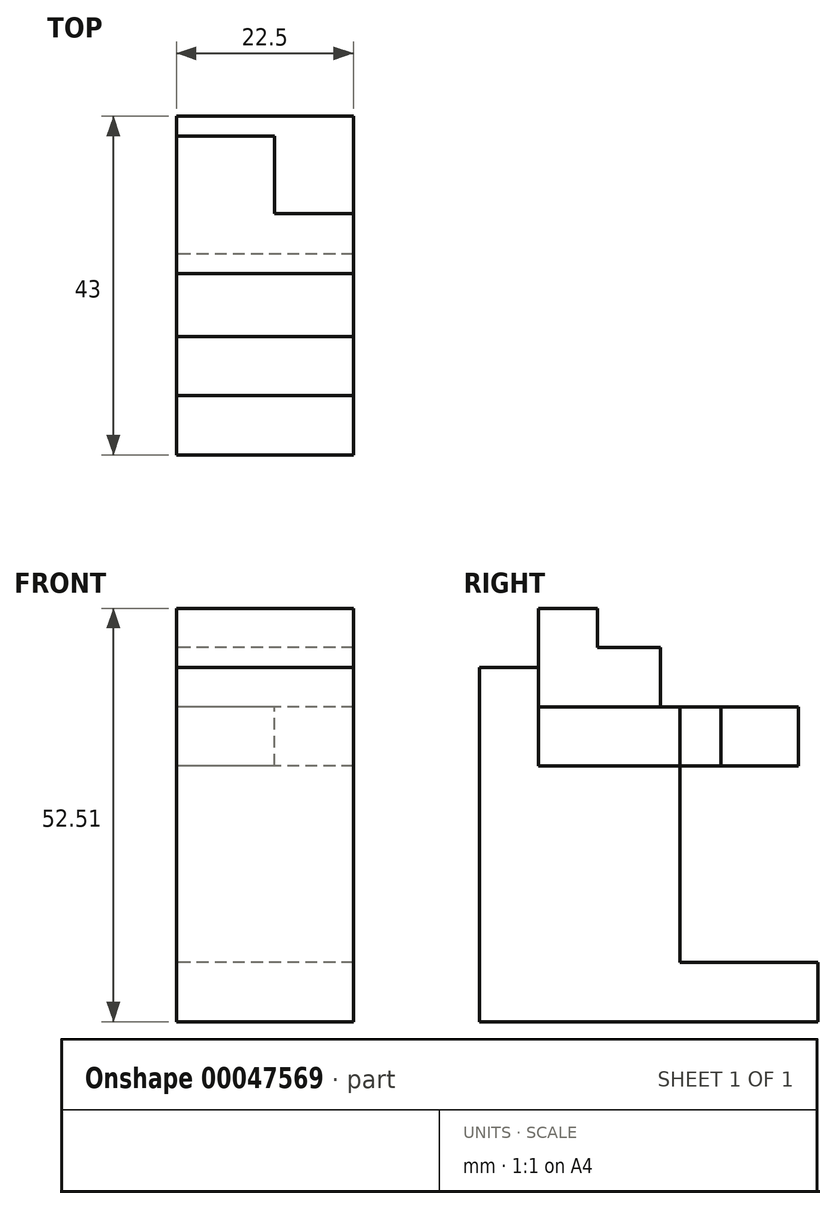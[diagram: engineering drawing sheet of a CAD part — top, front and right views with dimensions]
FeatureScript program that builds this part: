
annotation { "Feature Type Name" : "Feature", "Feature Type Description" : "" }
export const myFeature = defineFeature(function(context is Context, id is Id, definition is map)
    precondition{}
    {
        {
            var Q0;
            Q0=qCreatedBy(makeId("Right.planeOp"),FACE);
            var sketch = newSketch(context, id + "F0", { "sketchPlane" : qUnion([Q0])});
            skLineSegment(sketch, "E0", {"start": v(0, 0) * mm, "end": v(33, 0) * mm});
            skLineSegment(sketch, "E1", {"start": v(33, 0) * mm, "end": v(33, 7.5) * mm});
            skLineSegment(sketch, "E2", {"start": v(33, 7.5) * mm, "end": v(15.5, 7.5) * mm});
            skLineSegment(sketch, "E3", {"start": v(15.5, 7.5) * mm, "end": v(15.5, 15) * mm});
            skLineSegment(sketch, "E4", {"start": v(15.5, 15) * mm, "end": v(7.5, 15) * mm});
            skLineSegment(sketch, "E5", {"start": v(7.5, 15) * mm, "end": v(7.5, 20) * mm});
            skLineSegment(sketch, "E6", {"start": v(7.5, 20) * mm, "end": v(0, 20) * mm});
            skLineSegment(sketch, "E7", {"start": v(0, 20) * mm, "end": v(0, 0) * mm});
            skSolve(sketch);
        }
        {
            var Q0;
            Q0 = qSketchRegion(id + "F0", true);
            extrude(context, id + "F1", {"entities" : qUnion([Q0]), "depth" : 22.5 * mm});
        }
        {
            var Q0;
            Q0=makeQuery(id+"F1.opExtrude","SWEPT_FACE",FACE,{"disambiguationData":[OSD([sQuery(id+"F0.wireOp",EDGE,"E2")])]});
            var sketch = newSketch(context, id + "F2", { "sketchPlane" : qUnion([Q0])});
            skLineSegment(sketch, "E8.bottom", {"start": v(22.5, 33) * mm, "end": v(12.5, 33) * mm});
            skLineSegment(sketch, "E8.top", {"start": v(22.5, 23.16) * mm, "end": v(12.5, 23.16) * mm});
            skLineSegment(sketch, "E8.left", {"start": v(22.5, 33) * mm, "end": v(22.5, 23.16) * mm});
            skLineSegment(sketch, "E8.right", {"start": v(12.5, 33) * mm, "end": v(12.5, 23.16) * mm});
            skSolve(sketch);
        }
        {
            var Q0;
            Q0 = qSketchRegion(id + "F2", true);
            extrude(context, id + "F3", {"entities" : qUnion([Q0]), "operationType" : NewBodyOperationType.REMOVE, "oppositeDirection" : true, "depth" : 25 * mm});
        }
        {
            var Q0;
            Q0=qCreatedBy(makeId("Right.planeOp"),FACE);
            var sketch = newSketch(context, id + "F4", { "sketchPlane" : qUnion([Q0])});
            skLineSegment(sketch, "E9", {"start": v(-7.5, -32.5) * mm, "end": v(35.5, -32.5) * mm});
            skLineSegment(sketch, "E10", {"start": v(-7.5, -32.5) * mm, "end": v(-7.5, 12.5) * mm});
            skLineSegment(sketch, "E11", {"start": v(-7.5, 12.5) * mm, "end": v(0, 12.5) * mm});
            skLineSegment(sketch, "E12", {"start": v(0, 12.5) * mm, "end": v(0, 7.5) * mm});
            skLineSegment(sketch, "E13", {"start": v(35.5, -32.5) * mm, "end": v(35.5, -25) * mm});
            skLineSegment(sketch, "E14", {"start": v(35.5, -25) * mm, "end": v(18, -25) * mm});
            skLineSegment(sketch, "E15", {"start": v(0, 7.5) * mm, "end": v(18, 7.5) * mm});
            skLineSegment(sketch, "E16", {"start": v(18, 7.5) * mm, "end": v(18, -25) * mm});
            skSolve(sketch);
        }
        {
            var Q0;
            Q0 = qSketchRegion(id + "F4", true);
            extrude(context, id + "F5", {"entities" : qUnion([Q0]), "depth" : 22.5 * mm});
        }
    });
